# Revit family: Specialty_Equipment-Detroit_Radiant-Unit_Heater-DR_Series-bk1
name_source: partatom
category: Specialty Equipment
units: mm (PartAtom-declared; Revit-internal decimal feet)

## family parameters
Always vertical = Yes
Cut with Voids When Loaded = No
Enable Cutting in Views = No
Maintain Annotation Orientation = No
OmniClass Number = 23.75.00.00
OmniClass Title = Climate Control (HVAC)
Part Type = Normal
Room Calculation Point = No
Round Connector Dimension = Use Diameter
Shared = No
Work Plane-Based = Yes

## types (14) — shared parameters
Assembly Code = D3020
CD_Angle Max = 35.00°
CD_Angle Min = 20.00°
CD_Finish = Metal-Steel-Detroit_Radiant-Coated_Aluminized_Steel
CD_Finish Component = Metal-Steel-Detroit_Radiant-Stainless
CD_Heater Angle Calc = 30.00°
CD_Install Documentation = https://www.reverberray.com
CD_Microsite = https://www.caddetails.com
CD_Product Documentation Link = https://www.reverberray.com
CD_Product Name = High-Intensity, Gas-Fired, Infared Heaters
CD_Product Page URL = https://www.reverberray.com
CD_Requested Heater Angle = 30.00°
CD_Unit Size = Description of Product Sizing, set with equation if possible
Description = High-Intensity, Gas-Fired, Infared Heaters
Manufacturer = Detroit Radiant Products Company
URL = https://www.reverberray.com
zero-valued in all types: Default Elevation

## per-type parameters (varying)
| type | CD_Gas Connector | CD_Heater Type |
| DR-30 | 30,000 BTU | Specialty_Equipment-Detroit_Radiant-Unit_Heater-DR_Series_Nested : DR-30 |
| DR-30(S) | 30,000 BTU | Specialty_Equipment-Detroit_Radiant-Unit_Heater-DR_Series_Nested : DR-30(S) |
| DR-45 | 45,000 BTU | Specialty_Equipment-Detroit_Radiant-Unit_Heater-DR_Series_Nested : DR-45 |
| DR-50 | 50,000 BTU | Specialty_Equipment-Detroit_Radiant-Unit_Heater-DR_Series_Nested : DR-50 |
| DR-55 | 55,000 BTU | Specialty_Equipment-Detroit_Radiant-Unit_Heater-DR_Series_Nested : DR-55 |
| DR-60 | 60,000 BTU | Specialty_Equipment-Detroit_Radiant-Unit_Heater-DR_Series_Nested : DR-60 |
| DR-75 | 75,000 BTU | Specialty_Equipment-Detroit_Radiant-Unit_Heater-DR_Series_Nested : DR-75 |
| DR-80 | 80,000 BTU | Specialty_Equipment-Detroit_Radiant-Unit_Heater-DR_Series_Nested : DR-80 |
| DR-85 | 85,000 BTU | Specialty_Equipment-Detroit_Radiant-Unit_Heater-DR_Series_Nested : DR-85 |
| DR-90 | 90,000 BTU | Specialty_Equipment-Detroit_Radiant-Unit_Heater-DR_Series_Nested : DR-90 |
| DR-95 | 95,000 BTU | Specialty_Equipment-Detroit_Radiant-Unit_Heater-DR_Series_Nested : DR-95 |
| DR-100 | 100,000 BTU | Specialty_Equipment-Detroit_Radiant-Unit_Heater-DR_Series_Nested : DR-100 |
| DR-130 | 130,000 BTU | Specialty_Equipment-Detroit_Radiant-Unit_Heater-DR_Series_Nested : DR-130 |
| DR-160 | 160,000 BTU | Specialty_Equipment-Detroit_Radiant-Unit_Heater-DR_Series_Nested : DR-160 |

note: column(s) folded — value = type name in every type: Model

## geometry (parser evidence)
native form markers: Sweep x4
no freeform markers — native parametric forms only
